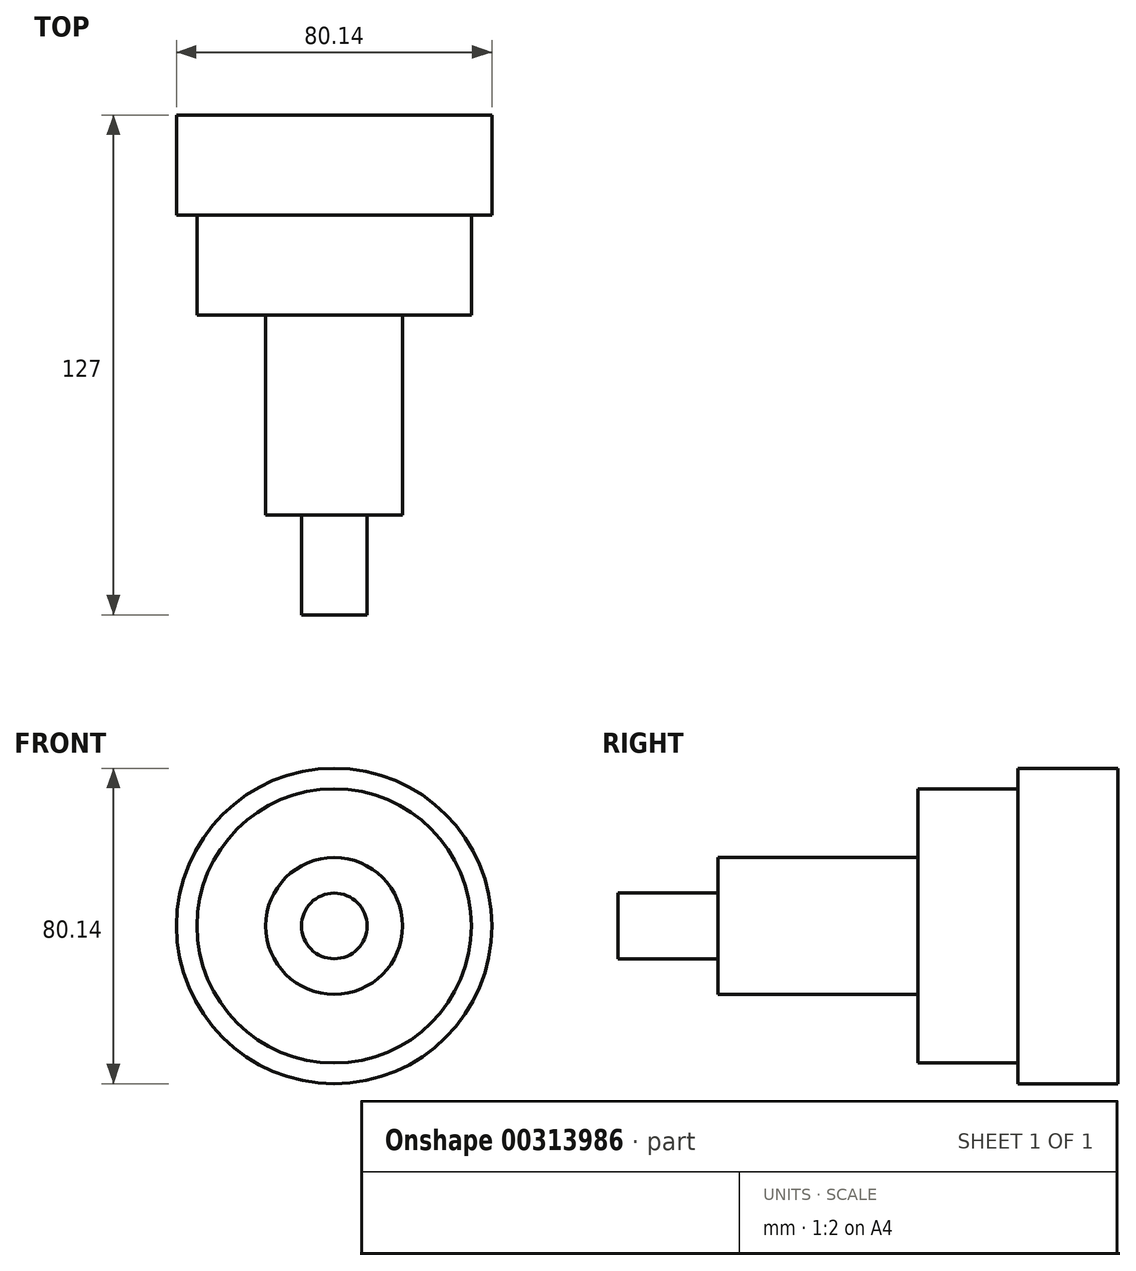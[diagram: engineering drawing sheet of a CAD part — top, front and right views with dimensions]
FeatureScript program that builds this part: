
annotation { "Feature Type Name" : "Feature", "Feature Type Description" : "" }
export const myFeature = defineFeature(function(context is Context, id is Id, definition is map)
    precondition{}
    {
        {
            var Q0;
            Q0=qCreatedBy(makeId("Front.planeOp"),FACE);
            var sketch = newSketch(context, id + "F0", { "sketchPlane" : qUnion([Q0])});
            skCircle(sketch, "E0", {"center": v(0, 0) * mm, "radius": 40.07 * mm});
            skCircle(sketch, "E1", {"center": v(0, 0) * mm, "radius": 34.85 * mm});
            skCircle(sketch, "E2", {"center": v(0, 0) * mm, "radius": 17.39 * mm});
            skCircle(sketch, "E3", {"center": v(0, 0) * mm, "radius": 8.34 * mm});
            skSolve(sketch);
        }
        {
            var Q0;
            Q0=makeQuery(id+"F0.imprint","IMPRINT",FACE,{"disambiguationData":[TD([[makeQuery(id+"F0.imprint","IMPRINT",EDGE,{"derivedFrom":sQuery(id+"F0.wireOp",EDGE,"E0")}),1.0]])]});
            extrude(context, id + "F1", {"entities" : qUnion([Q0]), "depth" : 25.4 * mm});
        }
        {
            var Q0;
            Q0=makeQuery(id+"F0.imprint","IMPRINT",FACE,{"disambiguationData":[TD([[makeQuery(id+"F0.imprint","IMPRINT",EDGE,{"derivedFrom":sQuery(id+"F0.wireOp",EDGE,"E1")}),1.0]])]});
            extrude(context, id + "F2", {"entities" : qUnion([Q0]), "operationType" : NewBodyOperationType.ADD, "depth" : 50.8 * mm});
        }
        {
            var Q0;
            Q0=makeQuery(id+"F0.imprint","IMPRINT",FACE,{"disambiguationData":[TD([[makeQuery(id+"F0.imprint","IMPRINT",EDGE,{"derivedFrom":sQuery(id+"F0.wireOp",EDGE,"E2")}),1.0]])]});
            extrude(context, id + "F3", {"entities" : qUnion([Q0]), "operationType" : NewBodyOperationType.ADD, "depth" : 101.6 * mm});
        }
        {
            var Q0;
            Q0=makeQuery(id+"F0.imprint","IMPRINT",FACE,{"disambiguationData":[TD([[makeQuery(id+"F0.imprint","IMPRINT",EDGE,{"derivedFrom":sQuery(id+"F0.wireOp",EDGE,"E3")}),1.0]])]});
            extrude(context, id + "F4", {"entities" : qUnion([Q0]), "operationType" : NewBodyOperationType.ADD, "depth" : 127 * mm});
        }
    });
